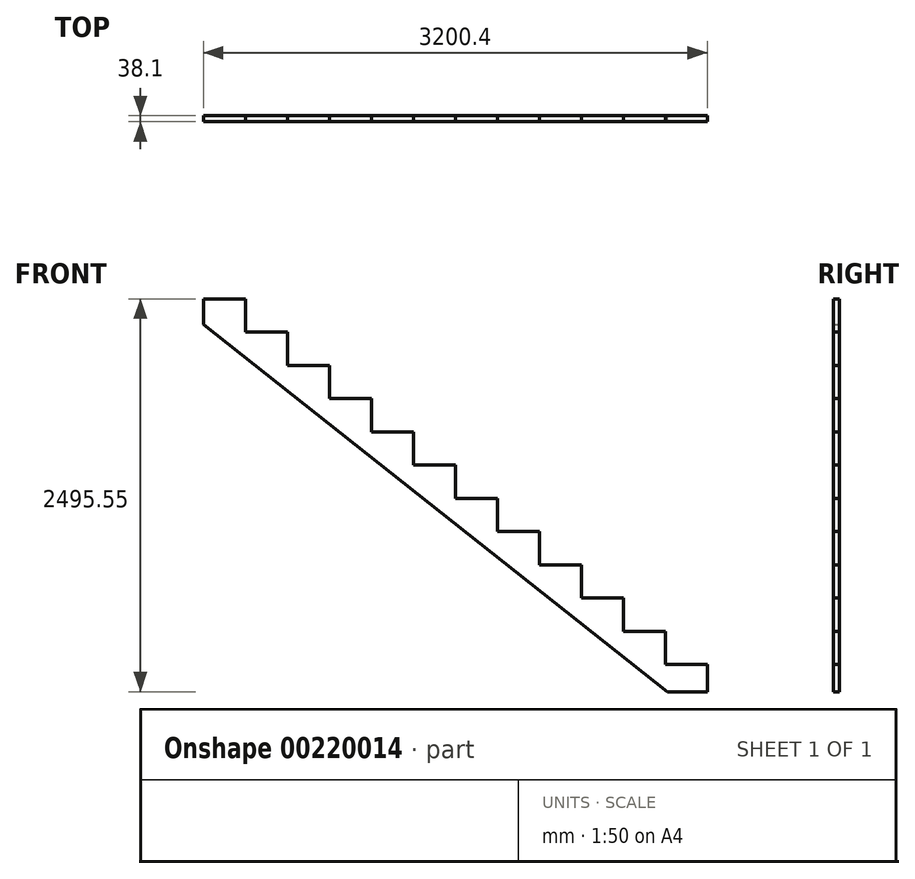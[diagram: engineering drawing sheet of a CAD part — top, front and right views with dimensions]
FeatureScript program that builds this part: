
annotation { "Feature Type Name" : "Feature", "Feature Type Description" : "" }
export const myFeature = defineFeature(function(context is Context, id is Id, definition is map)
    precondition{}
    {
        {
            var Q0;
            Q0=qCreatedBy(makeId("Front.planeOp"),FACE);
            var sketch = newSketch(context, id + "F0", { "sketchPlane" : qUnion([Q0])});
            skLineSegment(sketch, "E0", {"start": v(0, 0) * mm, "end": v(0, 173.04) * mm});
            skLineSegment(sketch, "E1", {"start": v(0, 173.04) * mm, "end": v(-266.7, 173.04) * mm});
            skLineSegment(sketch, "E2", {"start": v(-266.7, 173.04) * mm, "end": v(-266.7, 384.18) * mm});
            skLineSegment(sketch, "E3", {"start": v(-266.7, 384.18) * mm, "end": v(-533.4, 384.18) * mm});
            skLineSegment(sketch, "E4", {"start": v(-533.4, 384.18) * mm, "end": v(-533.4, 595.31) * mm});
            skLineSegment(sketch, "E5", {"start": v(-533.4, 595.31) * mm, "end": v(-800.1, 595.31) * mm});
            skLineSegment(sketch, "E6", {"start": v(-800.1, 595.31) * mm, "end": v(-800.1, 806.45) * mm});
            skLineSegment(sketch, "E7", {"start": v(-800.1, 806.45) * mm, "end": v(-1066.8, 806.45) * mm});
            skLineSegment(sketch, "E8", {"start": v(-1066.8, 806.45) * mm, "end": v(-1066.8, 1017.59) * mm});
            skLineSegment(sketch, "E9", {"start": v(-1066.8, 1017.59) * mm, "end": v(-1333.5, 1017.59) * mm});
            skLineSegment(sketch, "E10", {"start": v(-1333.5, 1017.59) * mm, "end": v(-1333.5, 1228.73) * mm});
            skLineSegment(sketch, "E11", {"start": v(-1333.5, 1228.73) * mm, "end": v(-1600.2, 1228.73) * mm});
            skLineSegment(sketch, "E12", {"start": v(-1600.2, 1228.73) * mm, "end": v(-1600.2, 1439.86) * mm});
            skLineSegment(sketch, "E13", {"start": v(-1600.2, 1439.86) * mm, "end": v(-1866.9, 1439.86) * mm});
            skLineSegment(sketch, "E14", {"start": v(-1866.9, 1651) * mm, "end": v(-2133.6, 1651) * mm});
            skLineSegment(sketch, "E15", {"start": v(-2133.6, 1651) * mm, "end": v(-2133.6, 1862.14) * mm});
            skLineSegment(sketch, "E16", {"start": v(-2133.6, 1862.14) * mm, "end": v(-2400.3, 1862.14) * mm});
            skLineSegment(sketch, "E17", {"start": v(-2400.3, 1862.14) * mm, "end": v(-2400.3, 2073.28) * mm});
            skLineSegment(sketch, "E18", {"start": v(-2400.3, 2073.28) * mm, "end": v(-2667, 2073.28) * mm});
            skLineSegment(sketch, "E19", {"start": v(-2667, 2073.28) * mm, "end": v(-2667, 2284.41) * mm});
            skLineSegment(sketch, "E20", {"start": v(-2667, 2284.41) * mm, "end": v(-2933.7, 2284.41) * mm});
            skLineSegment(sketch, "E21", {"start": v(-2933.7, 2284.41) * mm, "end": v(-2933.7, 2495.55) * mm});
            skLineSegment(sketch, "E22", {"start": v(-2933.7, 2495.55) * mm, "end": v(-3200.4, 2495.55) * mm});
            skLineSegment(sketch, "E23", {"start": v(-3200.4, 2334.13) * mm, "end": v(-3200.4, 2495.55) * mm});
            skLineSegment(sketch, "E24", {"start": v(-1866.9, 1439.86) * mm, "end": v(-1866.9, 1651) * mm});
            skLineSegment(sketch, "E25", {"start": v(-3200.4, 2334.13) * mm, "end": v(-252.02, 0) * mm});
            skLineSegment(sketch, "E26", {"start": v(-252.02, 0) * mm, "end": v(0, 0) * mm});
            skLineSegment(sketch, "E27", {"start": v(-2933.7, 2495.55) * mm, "end": v(-2133.6, 1862.14) * mm, "construction": true});
            skLineSegment(sketch, "E28", {"start": v(-1466.85, 1228.73) * mm, "end": v(-1466.85, 3057.53) * mm, "construction": true});
            skSolve(sketch);
        }
        {
            var Q0;
            Q0=makeQuery(id+"F0.imprint","IMPRINT",FACE,{"disambiguationData":[TD([[makeQuery(id+"F0.imprint","IMPRINT",EDGE,{"derivedFrom":sQuery(id+"F0.wireOp",EDGE,"E0")}),1.0]])]});
            extrude(context, id + "F1", {"entities" : qUnion([Q0]), "depth" : 38.1 * mm});
        }
    });
